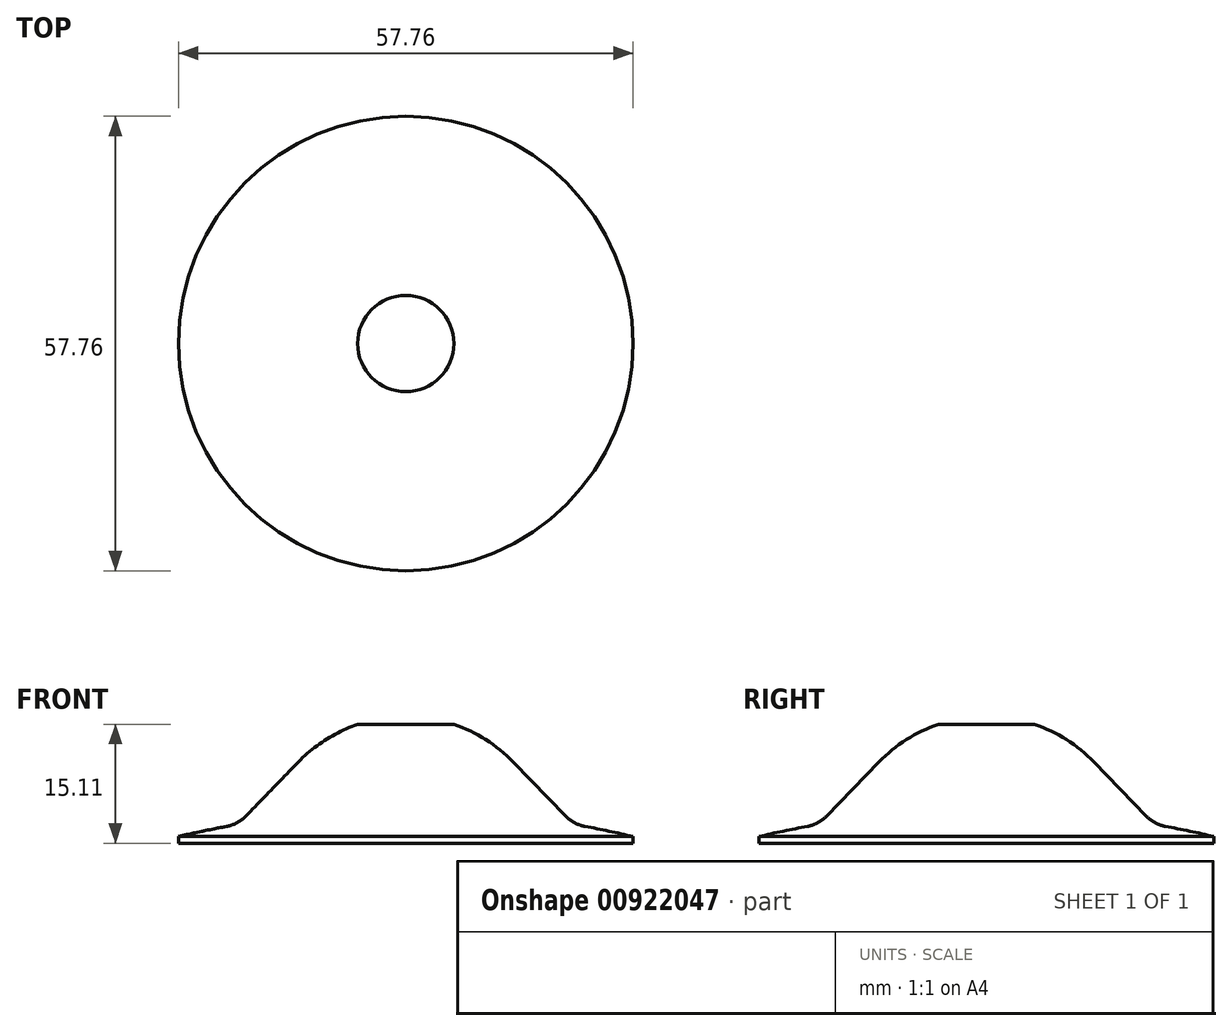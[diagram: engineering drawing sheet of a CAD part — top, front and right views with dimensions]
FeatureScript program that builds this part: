
annotation { "Feature Type Name" : "Feature", "Feature Type Description" : "" }
export const myFeature = defineFeature(function(context is Context, id is Id, definition is map)
    precondition{}
    {
        {
            var Q0;
            Q0=qCreatedBy(makeId("Front.planeOp"),FACE);
            var sketch = newSketch(context, id + "F0", { "sketchPlane" : qUnion([Q0])});
            skLineSegment(sketch, "E0.bottom", {"start": v(28.88, -0.42) * mm, "end": v(-28.88, -0.42) * mm});
            skLineSegment(sketch, "E0.top", {"start": v(28.88, 0.43) * mm, "end": v(-28.88, 0.42) * mm});
            skLineSegment(sketch, "E0.left", {"start": v(28.88, -0.42) * mm, "end": v(28.88, 0.43) * mm});
            skLineSegment(sketch, "E0.right", {"start": v(-28.88, -0.42) * mm, "end": v(-28.88, 0.43) * mm});
            skPoint(sketch, "E0.middle", {"position": v(0, 0) * mm});
            skArc(sketch, "E1", {"start": v(18.63, 0.43) * mm, "mid": v(0, 15.69) * mm, "end": v(-18.63, 0.43) * mm});
            skLineSegment(sketch, "E2", {"start": v(-13.64, 9.9) * mm, "end": v(-21.33, 1.97) * mm});
            skLineSegment(sketch, "E3", {"start": v(13.64, 9.9) * mm, "end": v(21.33, 1.97) * mm});
            skLineSegment(sketch, "E4", {"start": v(0, 0) * mm, "end": v(0, 20.8) * mm});
            skPoint(sketch, "E4.endSnap0", {"position": v(0, 3.33) * mm});
            skLineSegment(sketch, "E5", {"start": v(0, 0) * mm, "end": v(0, -3.31) * mm});
            skLineSegment(sketch, "E6", {"start": v(0, -3.31) * mm, "end": v(0, -166.6) * mm});
            skCircle(sketch, "E7", {"center": v(0, -121.2) * mm, "radius": 125 * mm});
            skCircle(sketch, "E8", {"center": v(-23.56, 6.15) * mm, "radius": 4.5 * mm});
            skSolve(sketch);
        }
        {
            var Q0;
            {var subQ0=sQuery(id+"F0.wireOp",EDGE,"E1");var subQ1=makeQuery(id+"F0.imprint","INTERSECT",VERTEX,{"derivedFrom":[subQ0,sQuery(id+"F0.wireOp",EDGE,"E2")]});Q0=makeQuery(id+"F0.imprint","IMPRINT",FACE,{"disambiguationData":[TD([[makeQuery(id+"F0.imprint","IMPRINT",EDGE,{"disambiguationData":[TD([[subQ1,1.0]])],"derivedFrom":subQ0}),1.0]])]});}
            var Q1;
            {var subQ0=sQuery(id+"F0.wireOp",EDGE,"E2");var subQ1=sQuery(id+"F0.wireOp",EDGE,"E1");var subQ2=makeQuery(id+"F0.imprint","INTERSECT",VERTEX,{"derivedFrom":[subQ1,subQ0]});Q1=makeQuery(id+"F0.imprint","IMPRINT",FACE,{"disambiguationData":[TD([[makeQuery(id+"F0.imprint","IMPRINT",EDGE,{"disambiguationData":[TD([[subQ2,-1.0]])],"derivedFrom":subQ1}),-1.0]])]});}
            var Q2;
            {var subQ3=sQuery(id+"F0.wireOp",EDGE,"E1");var subQ4=sQuery(id+"F0.wireOp",EDGE,"E0.top");var subQ5=makeQuery(id+"F0.imprint","INTERSECT",VERTEX,{"disambiguationData":[OD(1.0)],"derivedFrom":[subQ4,subQ3]});Q2=makeQuery(id+"F0.imprint","IMPRINT",FACE,{"disambiguationData":[TD([[makeQuery(id+"F0.imprint","IMPRINT",EDGE,{"disambiguationData":[TD([[subQ5,1.0]])],"derivedFrom":subQ3}),-1.0]])]});}
            var Q3;
            {var subQ0=sQuery(id+"F0.wireOp",EDGE,"E0.right");Q3=makeQuery(id+"F0.imprint","IMPRINT",FACE,{"disambiguationData":[TD([[makeQuery(id+"F0.imprint","IMPRINT",EDGE,{"derivedFrom":subQ0}),-1.0]])]});}
            var Q4;
            {var subQ0=sQuery(id+"F0.wireOp",EDGE,"E7");var subQ1=sQuery(id+"F0.wireOp",EDGE,"E2");var subQ2=makeQuery(id+"F0.imprint","INTERSECT",VERTEX,{"derivedFrom":[subQ1,subQ0]});Q4=makeQuery(id+"F0.imprint","IMPRINT",FACE,{"disambiguationData":[TD([[makeQuery(id+"F0.imprint","IMPRINT",EDGE,{"disambiguationData":[TD([[subQ2,1.0]])],"derivedFrom":subQ1}),-1.0]])]});}
            var Q5;
            {var subQ0=sQuery(id+"F0.wireOp",EDGE,"E1");var subQ1=sQuery(id+"F0.wireOp",EDGE,"E0.top");var subQ2=makeQuery(id+"F0.imprint","INTERSECT",VERTEX,{"disambiguationData":[OD(1.0)],"derivedFrom":[subQ1,subQ0]});Q5=makeQuery(id+"F0.imprint","IMPRINT",FACE,{"disambiguationData":[TD([[makeQuery(id+"F0.imprint","IMPRINT",EDGE,{"disambiguationData":[TD([[subQ2,1.0]])],"derivedFrom":subQ1}),-1.0]])]});}
            var Q6;
            Q6=sQuery(id+"F0.wireOp",EDGE,"E4");
            revolve(context, id + "F1", {"surfaceOperationType" : NewSurfaceOperationType.NEW, "entities" : qUnion([Q0, Q1, Q2, Q3, Q4, Q5]), "axis" : qUnion([Q6]), "revolveType" : RevolveType.FULL});
        }
        {
            var Q0;
            Q0=qCreatedBy(makeId("Right.planeOp"),FACE);
            var sketch = newSketch(context, id + "F2", { "sketchPlane" : qUnion([Q0])});
            skLineSegment(sketch, "E9", {"start": v(27.68, 14.68) * mm, "end": v(-34.82, 14.68) * mm});
            skLineSegment(sketch, "E10", {"start": v(27.68, 14.68) * mm, "end": v(-3.94, 26.8) * mm});
            skLineSegment(sketch, "E11", {"start": v(-3.94, 26.8) * mm, "end": v(-36.16, 14.68) * mm});
            skLineSegment(sketch, "E12", {"start": v(-36.16, 14.68) * mm, "end": v(-34.82, 14.68) * mm});
            skSolve(sketch);
        }
        {
            var Q0;
            Q0 = qSketchRegion(id + "F2", true);
            extrude(context, id + "F3", {"entities" : qUnion([Q0]), "operationType" : NewBodyOperationType.REMOVE, "endBound" : BoundingType.SYMMETRIC, "oppositeDirection" : true, "depth" : 25 * mm, "offsetDistance" : 25 * mm});
        }
    });
